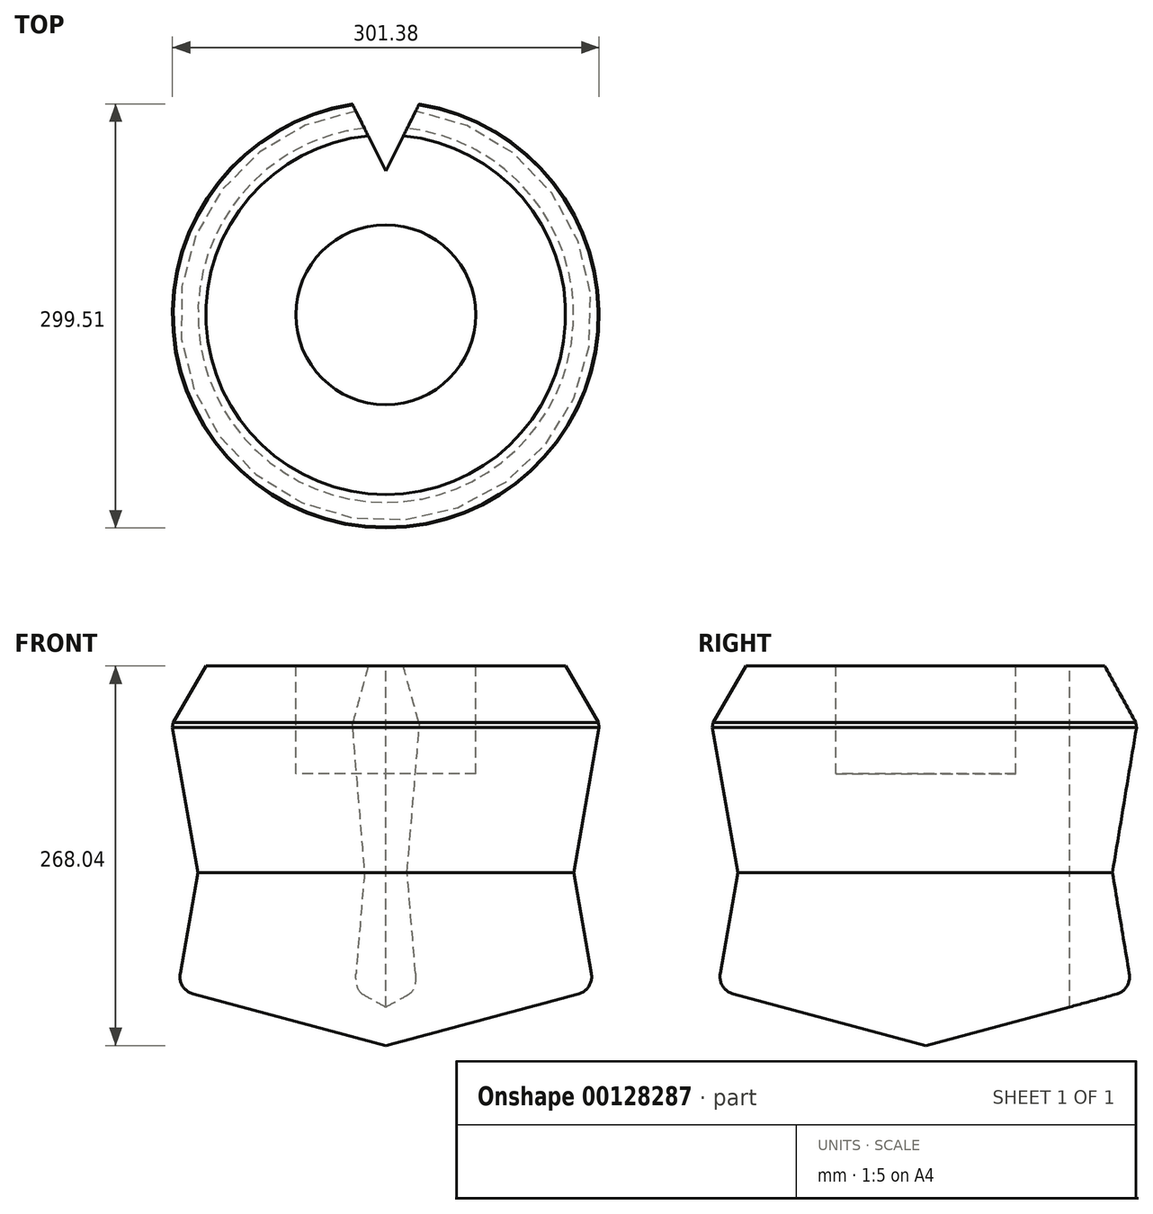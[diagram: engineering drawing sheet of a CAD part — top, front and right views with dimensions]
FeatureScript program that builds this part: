
annotation { "Feature Type Name" : "Feature", "Feature Type Description" : "" }
export const myFeature = defineFeature(function(context is Context, id is Id, definition is map)
    precondition{}
    {
        {
            var Q0;
            Q0=qCreatedBy(makeId("Front.planeOp"),FACE);
            var sketch = newSketch(context, id + "F0", { "sketchPlane" : qUnion([Q0])});
            skLineSegment(sketch, "E0", {"start": v(0, 0) * mm, "end": v(0, 154.5) * mm});
            skLineSegment(sketch, "E1", {"start": v(0, 154.5) * mm, "end": v(127, 154.5) * mm});
            skLineSegment(sketch, "E2", {"start": v(127, 154.5) * mm, "end": v(151, 112.92) * mm});
            skLineSegment(sketch, "E3", {"start": v(151, 112.92) * mm, "end": v(132.62, 8.63) * mm});
            skLineSegment(sketch, "E4", {"start": v(132.62, 8.63) * mm, "end": v(147.2, -74.1) * mm});
            skLineSegment(sketch, "E5", {"start": v(147.2, -74.1) * mm, "end": v(0, -113.54) * mm});
            skLineSegment(sketch, "E6", {"start": v(0, -113.54) * mm, "end": v(0, 0) * mm});
            skSolve(sketch);
        }
        {
            var Q0;
            Q0 = qSketchRegion(id + "F0", true);
            var Q1;
            Q1=sQuery(id+"F0.wireOp",EDGE,"E0");
            revolve(context, id + "F1", {"entities" : qUnion([Q0]), "axis" : qUnion([Q1]), "revolveType" : RevolveType.FULL});
        }
        {
            var Q0;
            Q0=makeQuery(id+"F1.opRevolve","SWEPT_FACE",FACE,{"disambiguationData":[OSD([sQuery(id+"F0.wireOp",EDGE,"E1")])]});
            var sketch = newSketch(context, id + "F2", { "sketchPlane" : qUnion([Q0])});
            skCircle(sketch, "E7", {"center": v(0, 0) * mm, "radius": 63.5 * mm});
            skSolve(sketch);
        }
        {
            var Q0;
            Q0=makeQuery(id+"F1.opRevolve","SWEPT_EDGE",EDGE,{"disambiguationData":[OSD([sQuery(id+"F0.wireOp",EDGE,"E4"),sQuery(id+"F0.wireOp",EDGE,"E5")])]});
            fillet(context, id + "F3", {"entities" : qUnion([Q0]), "radius" : 12.7 * mm, "tangentPropagation" : true, "allowEdgeOverflow" : false});
        }
        {
            var Q0;
            Q0 = qSketchRegion(id + "F2", true);
            extrude(context, id + "F4", {"entities" : qUnion([Q0]), "operationType" : NewBodyOperationType.REMOVE, "oppositeDirection" : true, "depth" : 76.2 * mm});
        }
        {
            var Q0;
            Q0=makeQuery(id+"F1.opRevolve","SWEPT_EDGE",EDGE,{"disambiguationData":[OSD([sQuery(id+"F0.wireOp",EDGE,"E2"),sQuery(id+"F0.wireOp",EDGE,"E3")])]});
            chamfer(context, id + "F5", {"entities" : qUnion([Q0]), "width" : 5.08 * mm, "tangentPropagation" : true});
        }
        {
            var Q0;
            Q0=makeQuery(id+"F1.opRevolve","SWEPT_FACE",FACE,{"disambiguationData":[OSD([sQuery(id+"F0.wireOp",EDGE,"E1")])]});
            var sketch = newSketch(context, id + "F6", { "sketchPlane" : qUnion([Q0])});
            skLineSegment(sketch, "E8", {"start": v(0, 0) * mm, "end": v(0, 101.6) * mm, "construction": true});
            skLineSegment(sketch, "E9", {"start": v(0, 101.6) * mm, "end": v(38.1, 177.8) * mm});
            skLineSegment(sketch, "E10", {"start": v(38.1, 177.8) * mm, "end": v(-38.1, 177.8) * mm});
            skLineSegment(sketch, "E11", {"start": v(-38.1, 177.8) * mm, "end": v(0, 101.6) * mm});
            skPoint(sketch, "E12", {"position": v(0, 177.8) * mm});
            skSolve(sketch);
        }
        {
            var Q0;
            Q0 = qSketchRegion(id + "F6", true);
            extrude(context, id + "F7", {"entities" : qUnion([Q0]), "operationType" : NewBodyOperationType.REMOVE, "endBound" : BoundingType.THROUGH_ALL, "oppositeDirection" : true, "depth" : 25.4 * mm});
        }
    });
